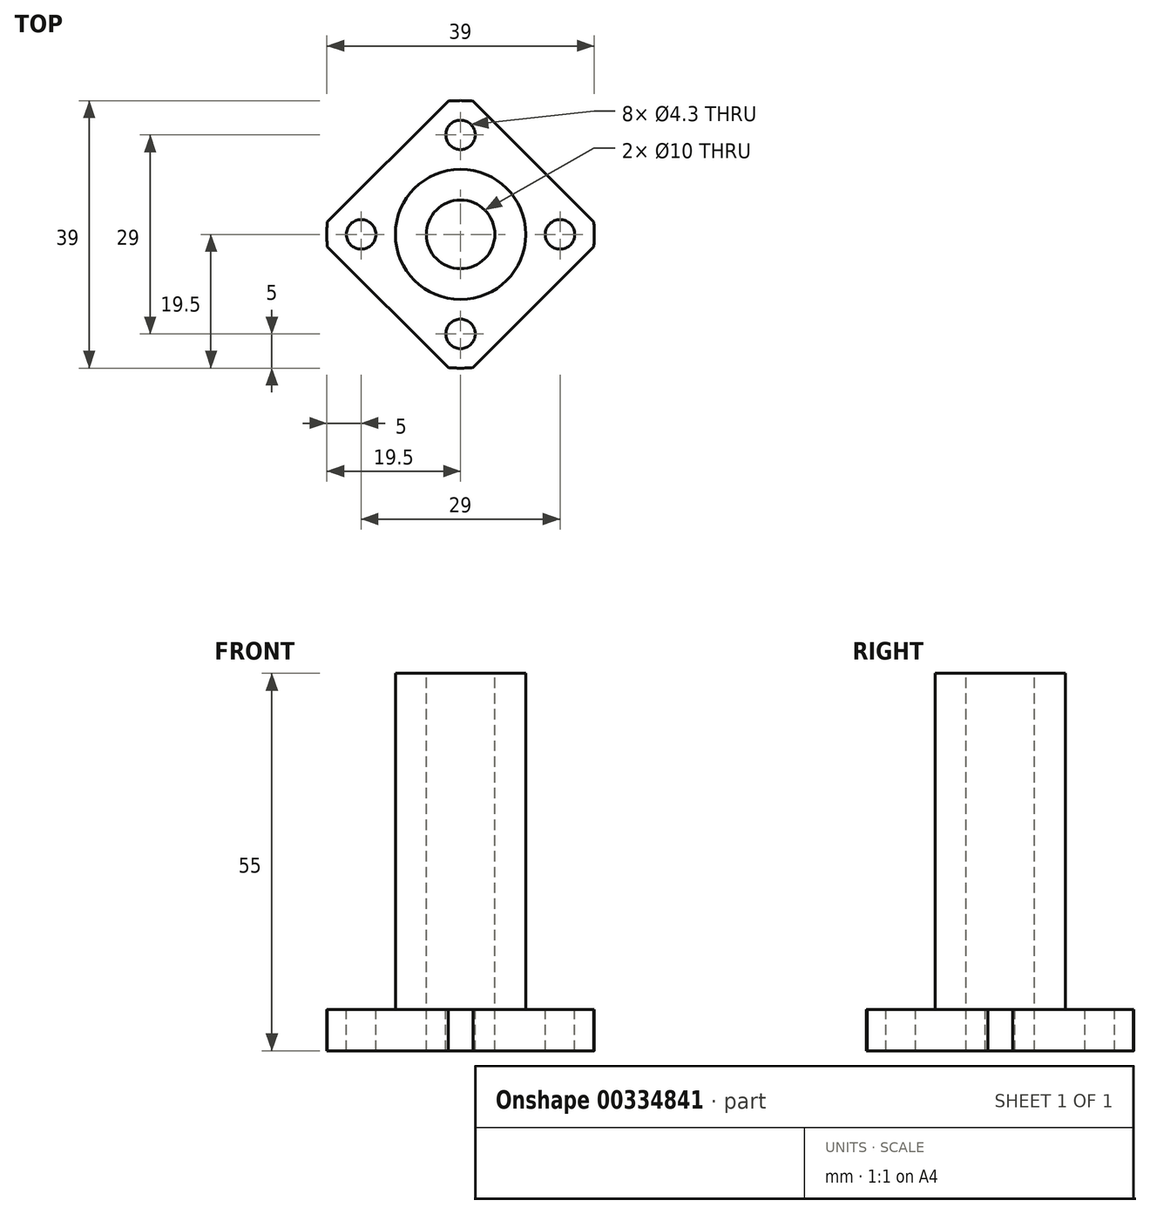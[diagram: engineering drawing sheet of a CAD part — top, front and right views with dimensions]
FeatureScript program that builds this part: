
annotation { "Feature Type Name" : "Feature", "Feature Type Description" : "" }
export const myFeature = defineFeature(function(context is Context, id is Id, definition is map)
    precondition{}
    {
        {
            var Q0;
            Q0=qCreatedBy(makeId("Top.planeOp"),FACE);
            var sketch = newSketch(context, id + "F0", { "sketchPlane" : qUnion([Q0])});
            skCircle(sketch, "E0", {"center": v(0, 0) * mm, "radius": 19.5 * mm});
            skSolve(sketch);
        }
        {
            var Q0;
            Q0 = qSketchRegion(id + "F0", true);
            extrude(context, id + "F1", {"entities" : qUnion([Q0]), "depth" : 6 * mm});
        }
        {
            var Q0;
            Q0=makeQuery(id+"F1.opExtrude","CAP_FACE",FACE,{"disambiguationData":[OSD([sQuery(id+"F0.wireOp",EDGE,"E0")])],"isStart":false});
            var sketch = newSketch(context, id + "F2", { "sketchPlane" : qUnion([Q0])});
            skCircle(sketch, "E1", {"center": v(0, 0) * mm, "radius": 9.5 * mm});
            skSolve(sketch);
        }
        {
            var Q0;
            Q0 = qSketchRegion(id + "F2", true);
            extrude(context, id + "F3", {"entities" : qUnion([Q0]), "operationType" : NewBodyOperationType.ADD, "depth" : (55 - 6) * mm});
        }
        {
            var Q0;
            Q0=makeQuery(id+"F3.opExtrude","CAP_FACE",FACE,{"disambiguationData":[OSD([sQuery(id+"F2.wireOp",EDGE,"E1")])],"isStart":false});
            var sketch = newSketch(context, id + "F4", { "sketchPlane" : qUnion([Q0])});
            skCircle(sketch, "E2", {"center": v(0, 0) * mm, "radius": 5 * mm});
            skSolve(sketch);
        }
        {
            var Q0;
            Q0 = qSketchRegion(id + "F4", true);
            extrude(context, id + "F5", {"entities" : qUnion([Q0]), "operationType" : NewBodyOperationType.REMOVE, "endBound" : BoundingType.THROUGH_ALL, "oppositeDirection" : true, "depth" : 25 * mm});
        }
        {
            var Q0;
            Q0=makeQuery(id+"F1.opExtrude","CAP_FACE",FACE,{"disambiguationData":[OSD([sQuery(id+"F0.wireOp",EDGE,"E0")])],"isStart":false});
            var sketch = newSketch(context, id + "F6", { "sketchPlane" : qUnion([Q0])});
            skCircle(sketch, "E3", {"center": v(0, 14.5) * mm, "radius": 2.15 * mm});
            skCircle(sketch, "E4.1.0", {"center": v(-14.5, 0) * mm, "radius": 2.15 * mm});
            skCircle(sketch, "E4.2.0", {"center": v(0, -14.5) * mm, "radius": 2.15 * mm});
            skCircle(sketch, "E4.3.0", {"center": v(14.5, 0) * mm, "radius": 2.15 * mm});
            skPoint(sketch, "E4.center", {"position": v(0, 0) * mm});
            skSolve(sketch);
        }
        {
            var Q0;
            Q0 = qSketchRegion(id + "F6", true);
            extrude(context, id + "F7", {"entities" : qUnion([Q0]), "operationType" : NewBodyOperationType.REMOVE, "oppositeDirection" : true, "depth" : 25 * mm});
        }
        {
            var Q0;
            Q0=makeQuery(id+"F1.opExtrude","SWEPT_BODY",BODY,{"disambiguationData":[OSD([sQuery(id+"F0.wireOp",EDGE,"E0")])]});
            transform(context, id + "F8", {"entities" : qUnion([Q0]), "transformType" : TransformType.COPY});
        }
        {
            var Q0;
            Q0=qCreatedBy(makeId("Top.planeOp"),FACE);
            var sketch = newSketch(context, id + "F9", { "sketchPlane" : qUnion([Q0])});
            skLineSegment(sketch, "E5.bottom", {"start": v(21.21, 0) * mm, "end": v(0, 21.21) * mm});
            skLineSegment(sketch, "E5.top", {"start": v(0, -21.21) * mm, "end": v(-21.21, 0) * mm});
            skLineSegment(sketch, "E5.left", {"start": v(21.21, 0) * mm, "end": v(0, -21.21) * mm});
            skLineSegment(sketch, "E5.right", {"start": v(0, 21.21) * mm, "end": v(-21.21, 0) * mm});
            skPoint(sketch, "E5.middle", {"position": v(0, 0) * mm});
            skLineSegment(sketch, "E6", {"start": v(0, 33.66) * mm, "end": v(0, 28.47) * mm, "construction": true});
            skSolve(sketch);
        }
        {
            var Q0;
            Q0 = qSketchRegion(id + "F9", true);
            extrude(context, id + "F10", {"entities" : qUnion([Q0]), "operationType" : NewBodyOperationType.INTERSECT, "depth" : 59.2 * mm});
        }
    });
